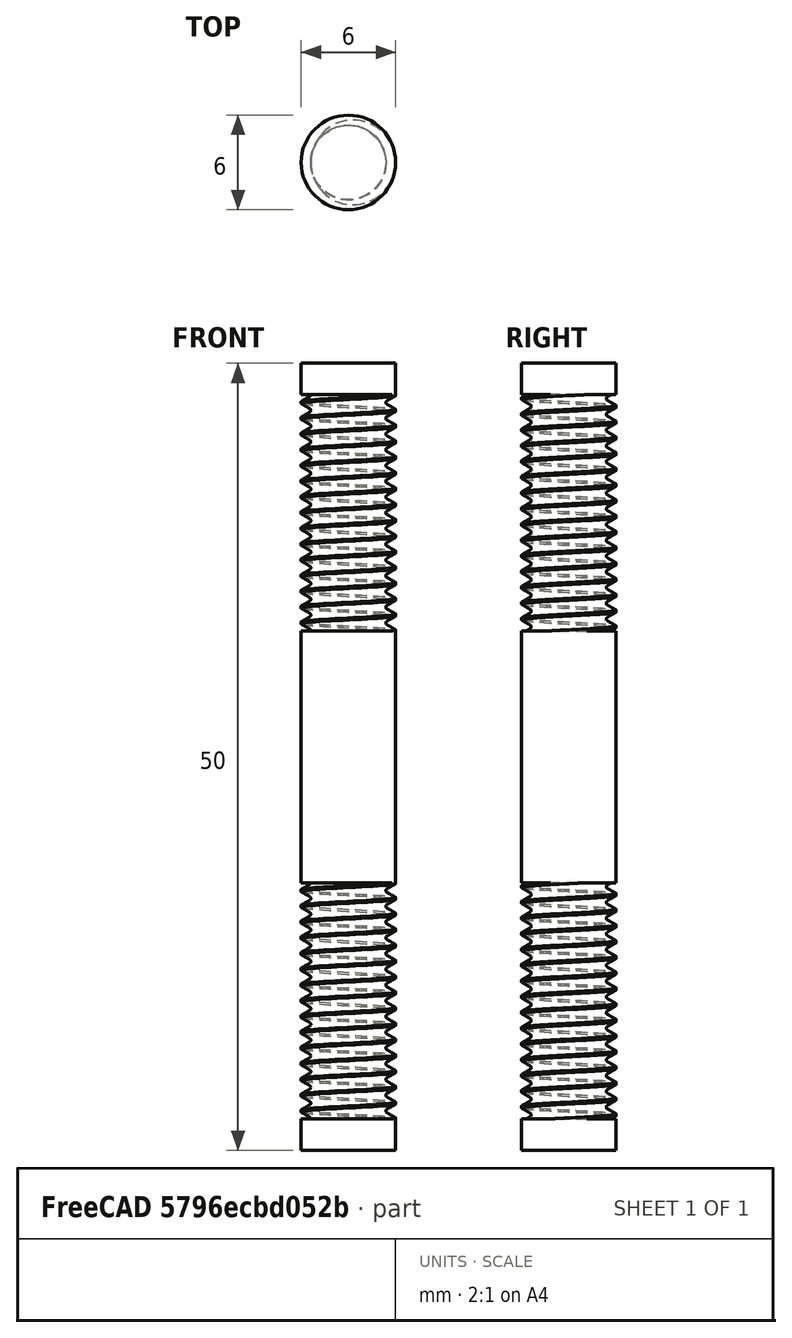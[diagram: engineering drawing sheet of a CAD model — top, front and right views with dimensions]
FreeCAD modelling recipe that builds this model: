
FCSTD DOCUMENT  (FreeCAD 1.0R39319 (Git))
Label: Tension_Rod
License: All rights reserved
LicenseURL: https://en.wikipedia.org/wiki/All_rights_reserved
objects: Part::FeaturePython×2, Part::Cut×2, Sketcher::SketchObject×1, PartDesign::Body×1, PartDesign::Pad×1
note: 10 computed .brp shape members not serialized (recipe doc carries the construction recipe); baked Part::Feature solids carry a one-line shape summary decoded from their .brp

FEATURE [Sketcher::SketchObject] Sketch
  ArcFitTolerance = 1e-06
  AttachmentSupport = -> [XY_Plane]
  FullyConstrained = true
  MakeInternals = false
  MapMode = 5
  sketch-geometry (1):
    g0: Circle CenterX=0 CenterY=0 CenterZ=0 NormalX=0 NormalY=0 NormalZ=1 AngleXU=0 Radius=3
  constraints (2):
    c: Coincident(g0,g-1)
    c: Diameter(g0) = 6
FEATURE [PartDesign::Body] Body
  AllowCompound = false
  Group = -> [Sketch]
  Origin = -> Origin
FEATURE [PartDesign::Pad] Pad
  Direction = (0,0,1)
  Length = 50
  Length2 = 10
  Profile = -> Sketch
  ReferenceAxis = -> Sketch [N_Axis]
  Refine = true
  Suppressed = false
  Type = 0
FEATURE [Part::FeaturePython] ScrewDie  label="M6x15-ScrewDie"  # WARN: FeaturePython — macro-defined, semantics opaque (R4)
  Diameter = 8
  DiameterCustom = 6
  Invert = false
  LeftHanded = false
  Length = 15
  MatchOuter = false
  OffsetAngle = 0
  PitchCustom = 1
  Placement = pos=(0,0,17) rot=(0,0,1;0rad)
  Thread = true
  Type = 0
FEATURE [Part::Cut] Cut
  Base = -> Pad
  Refine = true
  Tool = -> ScrewDie
FEATURE [Part::FeaturePython] ScrewDie001  label="M6x15-ScrewDie001"  # WARN: FeaturePython — macro-defined, semantics opaque (R4)
  Diameter = 8
  DiameterCustom = 6
  Invert = false
  LeftHanded = false
  Length = 15
  MatchOuter = false
  OffsetAngle = 0
  PitchCustom = 1
  Placement = pos=(0,0,48) rot=(0,0,1;0rad)
  Thread = true
  Type = 0
FEATURE [Part::Cut] Cut001
  Base = -> Cut
  Refine = true
  Tool = -> ScrewDie001
